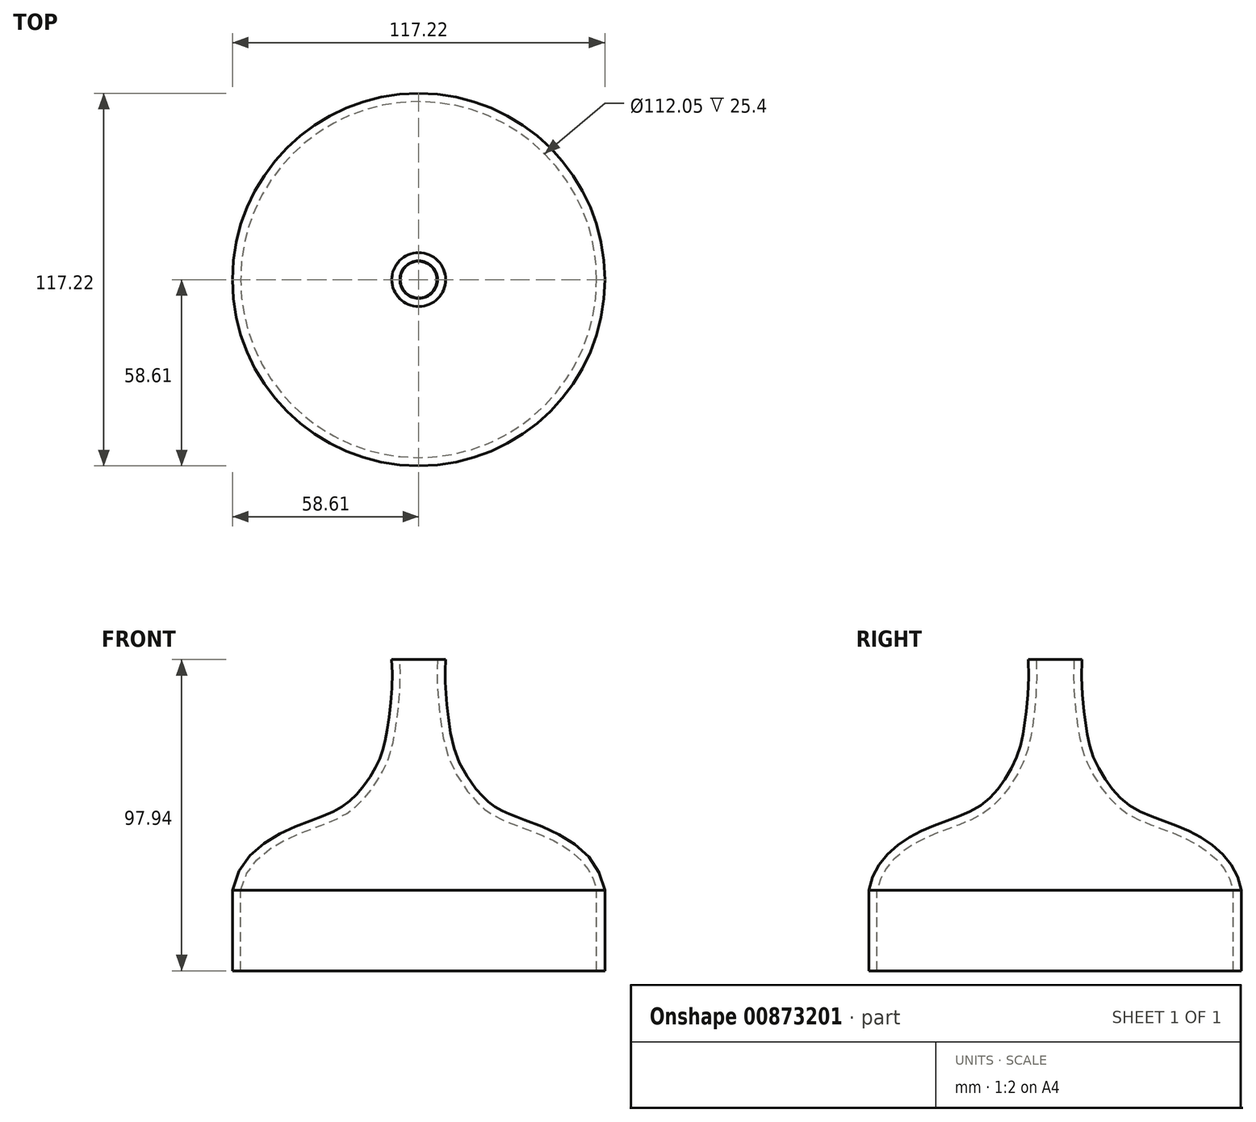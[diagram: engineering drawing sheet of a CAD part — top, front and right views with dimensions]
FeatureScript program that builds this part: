
annotation { "Feature Type Name" : "Feature", "Feature Type Description" : "" }
export const myFeature = defineFeature(function(context is Context, id is Id, definition is map)
    precondition{}
    {
        {
            var Q0;
            Q0=qCreatedBy(makeId("Front.planeOp"),FACE);
            var sketch = newSketch(context, id + "F0", { "sketchPlane" : qUnion([Q0])});
            skLineSegment(sketch, "E0", {"start": v(0, 0) * mm, "end": v(0, 72.54) * mm});
            skLineSegment(sketch, "E1", {"start": v(0, 72.54) * mm, "end": v(8.48, 72.54) * mm});
            skLineSegment(sketch, "E2", {"start": v(58.61, 0) * mm, "end": v(0, 0) * mm});
            skFitSpline(sketch, "E3", {"points": [v(58.61, 0) * mm, v(32.54, 22.4) * mm, v(21.14, 28.48) * mm, v(13.3, 39.12) * mm, v(10, 49.75) * mm, v(8.48, 72.54) * mm], "startDerivative": vector(-28.68, 154.57) * mm, "endDerivative": vector(7.26, 94.39) * mm});
            skLineSegment(sketch, "E4", {"start": v(8.48, 72.54) * mm, "end": v(8.48, 81.66) * mm});
            skSolve(sketch);
        }
        {
            var Q0;
            Q0 = qSketchRegion(id + "F0", true);
            var Q1;
            Q1=sQuery(id+"F0.wireOp",EDGE,"E0");
            revolve(context, id + "F1", {"surfaceOperationType" : NewSurfaceOperationType.NEW, "entities" : qUnion([Q0]), "axis" : qUnion([Q1]), "revolveType" : RevolveType.FULL});
        }
        {
            var Q0;
            Q0=makeQuery(id+"F1.opRevolve","SWEPT_FACE",FACE,{"disambiguationData":[OSD([sQuery(id+"F0.wireOp",EDGE,"E2")])]});
            var Q1;
            Q1=makeQuery(id+"F1.opRevolve","SWEPT_FACE",FACE,{"disambiguationData":[OSD([sQuery(id+"F0.wireOp",EDGE,"E1")])]});
            shell(context, id + "F2", {"entities" : qUnion([Q0, Q1]), "thickness" : 2.54 * mm});
        }
        {
            var Q0;
            Q0=makeQuery(id+"F1.opRevolve","SWEPT_FACE",FACE,{"disambiguationData":[OSD([sQuery(id+"F0.wireOp",EDGE,"E2")])]});
            extrude(context, id + "F3", {"entities" : qUnion([Q0]), "operationType" : NewBodyOperationType.ADD, "depth" : 25.4 * mm, "offsetDistance" : 25.4 * mm});
        }
    });
